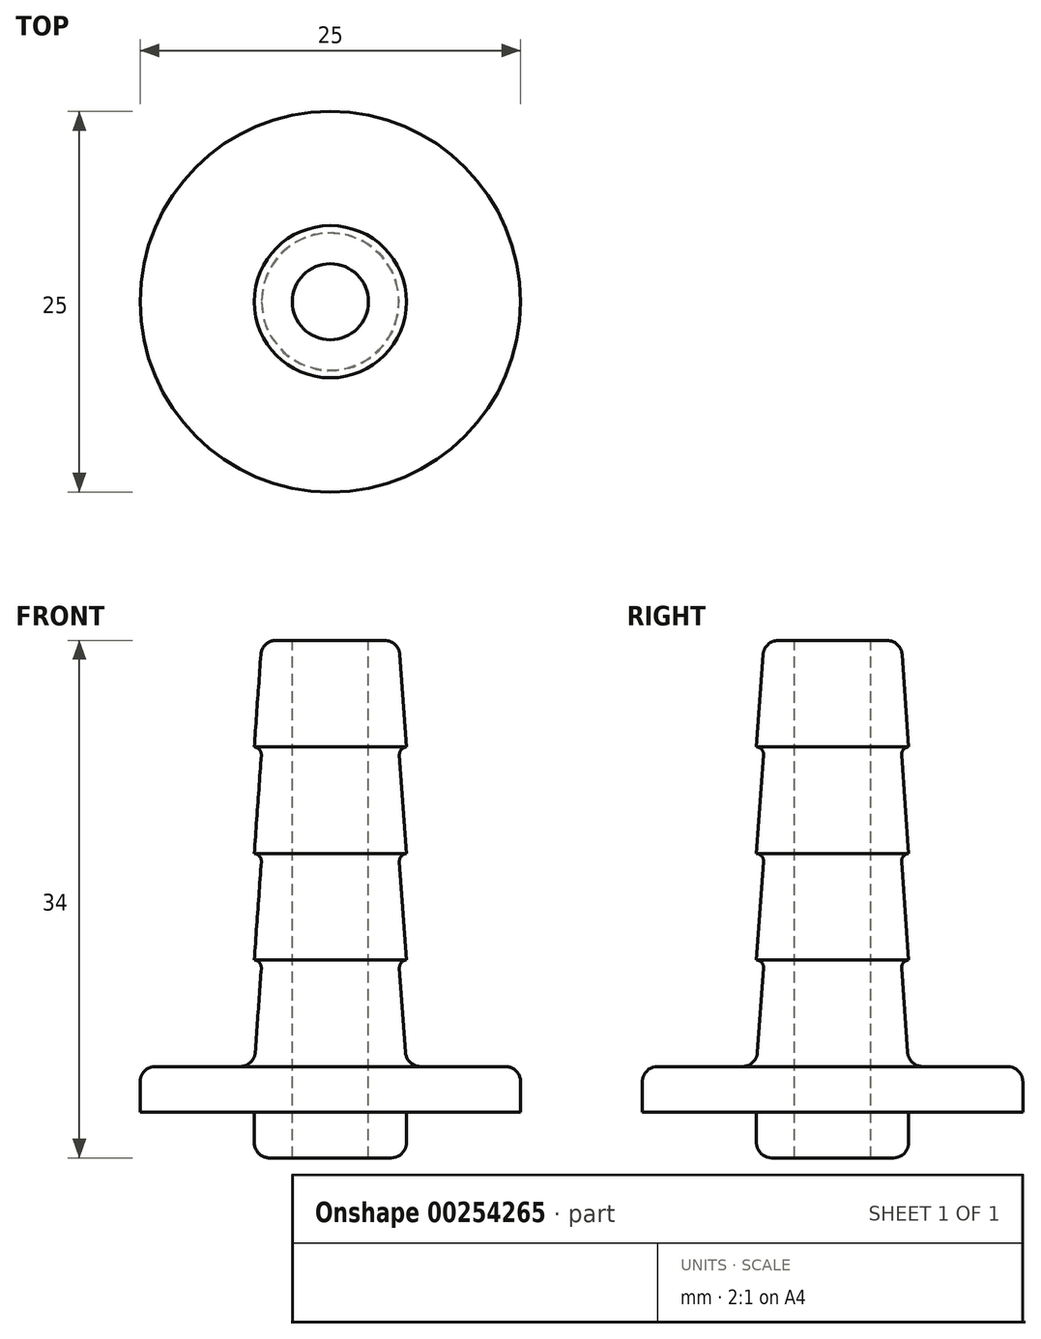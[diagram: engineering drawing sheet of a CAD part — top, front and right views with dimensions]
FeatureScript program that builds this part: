
annotation { "Feature Type Name" : "Feature", "Feature Type Description" : "" }
export const myFeature = defineFeature(function(context is Context, id is Id, definition is map)
    precondition{}
    {
        {
            var Q0;
            Q0=qCreatedBy(makeId("Front.planeOp"),FACE);
            var sketch = newSketch(context, id + "F0", { "sketchPlane" : qUnion([Q0])});
            skLineSegment(sketch, "E0", {"start": v(0, 28) * mm, "end": v(0, -13.74) * mm, "construction": true});
            skLineSegment(sketch, "E1", {"start": v(-4.5, 28) * mm, "end": v(-5, 21) * mm});
            skLineSegment(sketch, "E2", {"start": v(-4.5, 28) * mm, "end": v(0, 28) * mm});
            skLineSegment(sketch, "E3", {"start": v(-5, 21) * mm, "end": v(-4.5, 21) * mm});
            skLineSegment(sketch, "E4.0.1.0", {"start": v(-4.5, 21) * mm, "end": v(-5, 14) * mm});
            skLineSegment(sketch, "E4.0.1.1", {"start": v(-5, 14) * mm, "end": v(-4.5, 14) * mm});
            skLineSegment(sketch, "E4.0.2.0", {"start": v(-4.5, 14) * mm, "end": v(-5, 7) * mm});
            skLineSegment(sketch, "E4.0.2.1", {"start": v(-5, 7) * mm, "end": v(-4.5, 7) * mm});
            skLineSegment(sketch, "E4.0.3.0", {"start": v(-4.5, 7) * mm, "end": v(-5, 0) * mm});
            skLineSegment(sketch, "E4.direction1", {"start": v(-5, 21) * mm, "end": v(0, 21) * mm, "construction": true});
            skLineSegment(sketch, "E4.direction2", {"start": v(-5, 21) * mm, "end": v(-5, 14) * mm, "construction": true});
            skLineSegment(sketch, "E5", {"start": v(-5, 0) * mm, "end": v(-12.5, 0) * mm});
            skLineSegment(sketch, "E6", {"start": v(-12.5, 0) * mm, "end": v(-12.5, -3) * mm});
            skLineSegment(sketch, "E7", {"start": v(-12.5, -3) * mm, "end": v(-5, -3) * mm});
            skLineSegment(sketch, "E8", {"start": v(-5, -3) * mm, "end": v(-5, -6) * mm});
            skLineSegment(sketch, "E9", {"start": v(-5, -6) * mm, "end": v(0, -6) * mm});
            skLineSegment(sketch, "E10", {"start": v(0, 28) * mm, "end": v(0, -6) * mm});
            skSolve(sketch);
        }
        {
            var Q0;
            Q0=makeQuery(id+"F0.imprint","IMPRINT",FACE,{"disambiguationData":[TD([[makeQuery(id+"F0.imprint","IMPRINT",EDGE,{"derivedFrom":sQuery(id+"F0.wireOp",EDGE,"E1")}),1.0]])]});
            var Q1;
            Q1=sQuery(id+"F0.wireOp",EDGE,"E10");
            revolve(context, id + "F1", {"entities" : qUnion([Q0]), "axis" : qUnion([Q1]), "revolveType" : RevolveType.FULL});
        }
        {
            var Q0;
            Q0=makeQuery(id+"F1.opRevolve","SWEPT_FACE",FACE,{"disambiguationData":[OSD([sQuery(id+"F0.wireOp",EDGE,"E2")])]});
            var sketch = newSketch(context, id + "F2", { "sketchPlane" : qUnion([Q0])});
            skCircle(sketch, "E11", {"center": v(0, 0) * mm, "radius": 2.5 * mm});
            skSolve(sketch);
        }
        {
            var Q0;
            Q0=makeQuery(id+"F2.imprint","IMPRINT",FACE,{"disambiguationData":[TD([[makeQuery(id+"F2.imprint","IMPRINT",EDGE,{"derivedFrom":sQuery(id+"F2.wireOp",EDGE,"E11")}),1.0]])]});
            extrude(context, id + "F3", {"entities" : qUnion([Q0]), "operationType" : NewBodyOperationType.REMOVE, "endBound" : BoundingType.UP_TO_NEXT, "oppositeDirection" : true, "depth" : 25 * mm});
        }
        {
            var Q0;
            Q0=makeQuery(id+"F1.opRevolve","SWEPT_EDGE",EDGE,{"disambiguationData":[OSD([sQuery(id+"F0.wireOp",EDGE,"E3"),sQuery(id+"F0.wireOp",EDGE,"E4.0.1.0")])]});
            var Q1;
            Q1=makeQuery(id+"F1.opRevolve","SWEPT_EDGE",EDGE,{"disambiguationData":[OSD([sQuery(id+"F0.wireOp",EDGE,"E4.0.1.1"),sQuery(id+"F0.wireOp",EDGE,"E4.0.2.0")])]});
            var Q2;
            Q2=makeQuery(id+"F1.opRevolve","SWEPT_EDGE",EDGE,{"disambiguationData":[OSD([sQuery(id+"F0.wireOp",EDGE,"E4.0.2.1"),sQuery(id+"F0.wireOp",EDGE,"E4.0.3.0")])]});
            fillet(context, id + "F4", {"entities" : qUnion([Q0, Q1, Q2]), "radius" : .5 * mm, "tangentPropagation" : true, "allowEdgeOverflow" : false});
        }
        {
            var Q0;
            Q0=makeQuery(id+"F1.opRevolve","SWEPT_EDGE",EDGE,{"disambiguationData":[OSD([sQuery(id+"F0.wireOp",EDGE,"E1"),sQuery(id+"F0.wireOp",EDGE,"E2")])]});
            var Q1;
            Q1=makeQuery(id+"F1.opRevolve","SWEPT_EDGE",EDGE,{"disambiguationData":[OSD([sQuery(id+"F0.wireOp",EDGE,"E4.0.3.0"),sQuery(id+"F0.wireOp",EDGE,"E5")])]});
            var Q2;
            Q2=makeQuery(id+"F1.opRevolve","SWEPT_EDGE",EDGE,{"disambiguationData":[OSD([sQuery(id+"F0.wireOp",EDGE,"E8"),sQuery(id+"F0.wireOp",EDGE,"E9")])]});
            var Q3;
            Q3=makeQuery(id+"F1.opRevolve","SWEPT_EDGE",EDGE,{"disambiguationData":[OSD([sQuery(id+"F0.wireOp",EDGE,"E5"),sQuery(id+"F0.wireOp",EDGE,"E6")])]});
            fillet(context, id + "F5", {"entities" : qUnion([Q0, Q1, Q2, Q3]), "radius" : 1 * mm, "tangentPropagation" : true, "allowEdgeOverflow" : false});
        }
    });
